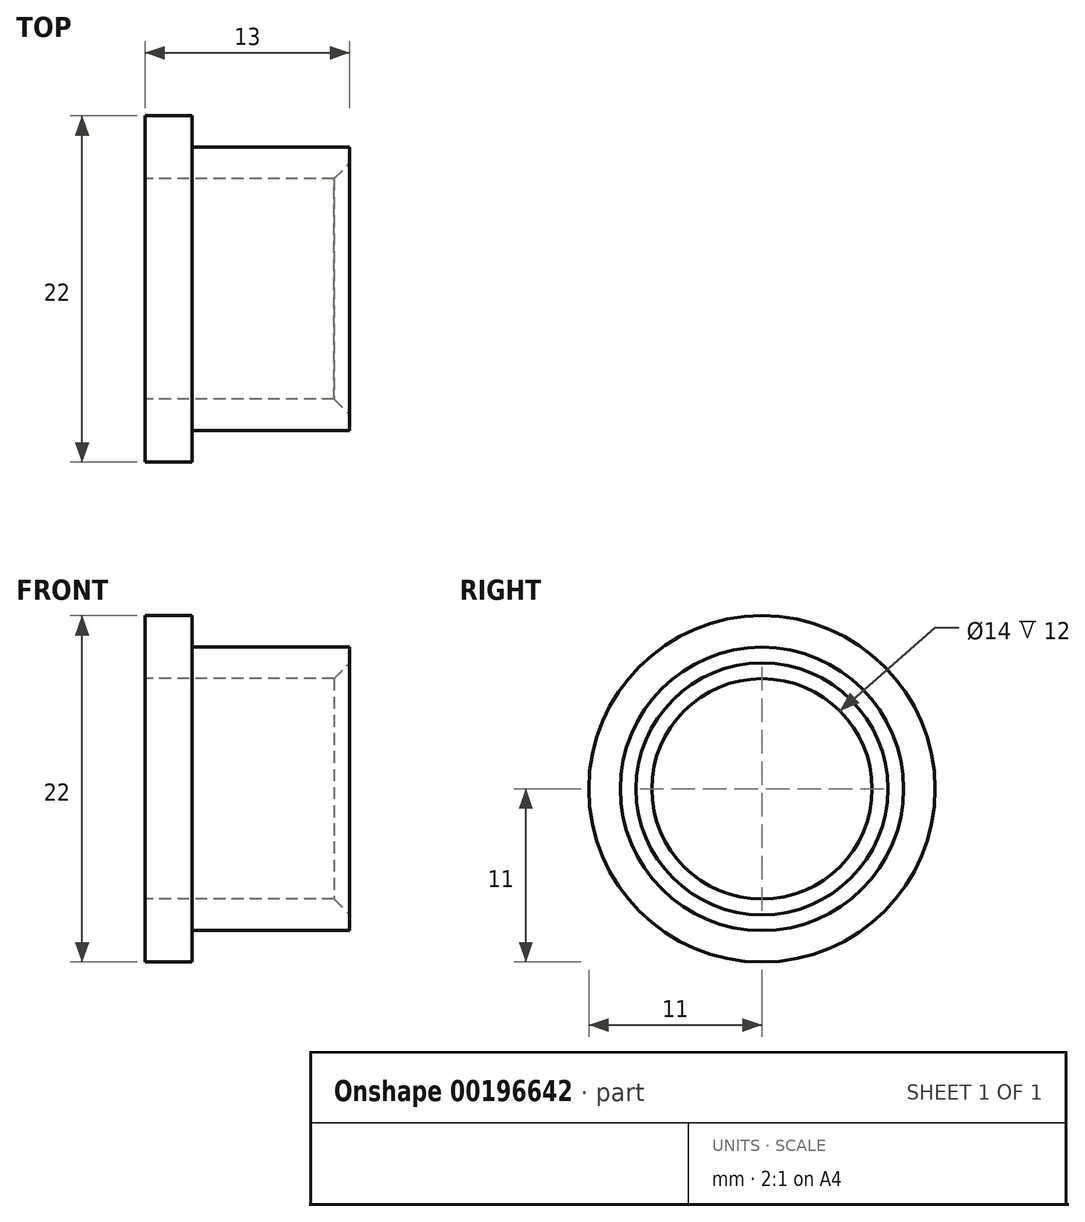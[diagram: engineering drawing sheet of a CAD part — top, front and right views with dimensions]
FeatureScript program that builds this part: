
annotation { "Feature Type Name" : "Feature", "Feature Type Description" : "" }
export const myFeature = defineFeature(function(context is Context, id is Id, definition is map)
    precondition{}
    {
        {
            var Q0;
            Q0=qCreatedBy(makeId("Front.planeOp"),FACE);
            var sketch = newSketch(context, id + "F0", { "sketchPlane" : qUnion([Q0])});
            skLineSegment(sketch, "E0", {"start": v(0, 7) * mm, "end": v(0, 11) * mm});
            skLineSegment(sketch, "E1", {"start": v(0, 11) * mm, "end": v(3, 11) * mm});
            skLineSegment(sketch, "E2", {"start": v(3, 11) * mm, "end": v(3, 9) * mm});
            skLineSegment(sketch, "E3", {"start": v(3, 9) * mm, "end": v(13, 9) * mm});
            skLineSegment(sketch, "E4", {"start": v(0, 7) * mm, "end": v(13, 7) * mm});
            skLineSegment(sketch, "E5", {"start": v(13, 7) * mm, "end": v(13, 9) * mm});
            skLineSegment(sketch, "E6", {"start": v(0, 0) * mm, "end": v(28.9, 0) * mm, "construction": true});
            skSolve(sketch);
        }
        {
            var Q0;
            Q0=makeQuery(id+"F0.imprint","IMPRINT",FACE,{"disambiguationData":[TD([[makeQuery(id+"F0.imprint","IMPRINT",EDGE,{"derivedFrom":sQuery(id+"F0.wireOp",EDGE,"E0")}),-1.0]])]});
            var Q1;
            Q1=sQuery(id+"F0.wireOp",EDGE,"E6");
            revolve(context, id + "F1", {"entities" : qUnion([Q0]), "axis" : qUnion([Q1]), "revolveType" : RevolveType.FULL});
        }
        {
            var Q0;
            Q0=makeQuery(id+"F1.opRevolve","SWEPT_EDGE",EDGE,{"disambiguationData":[OSD([sQuery(id+"F0.wireOp",EDGE,"E4"),sQuery(id+"F0.wireOp",EDGE,"E5")])]});
            chamfer(context, id + "F2", {"entities" : qUnion([Q0]), "width" : 1 * mm, "tangentPropagation" : true});
        }
    });
